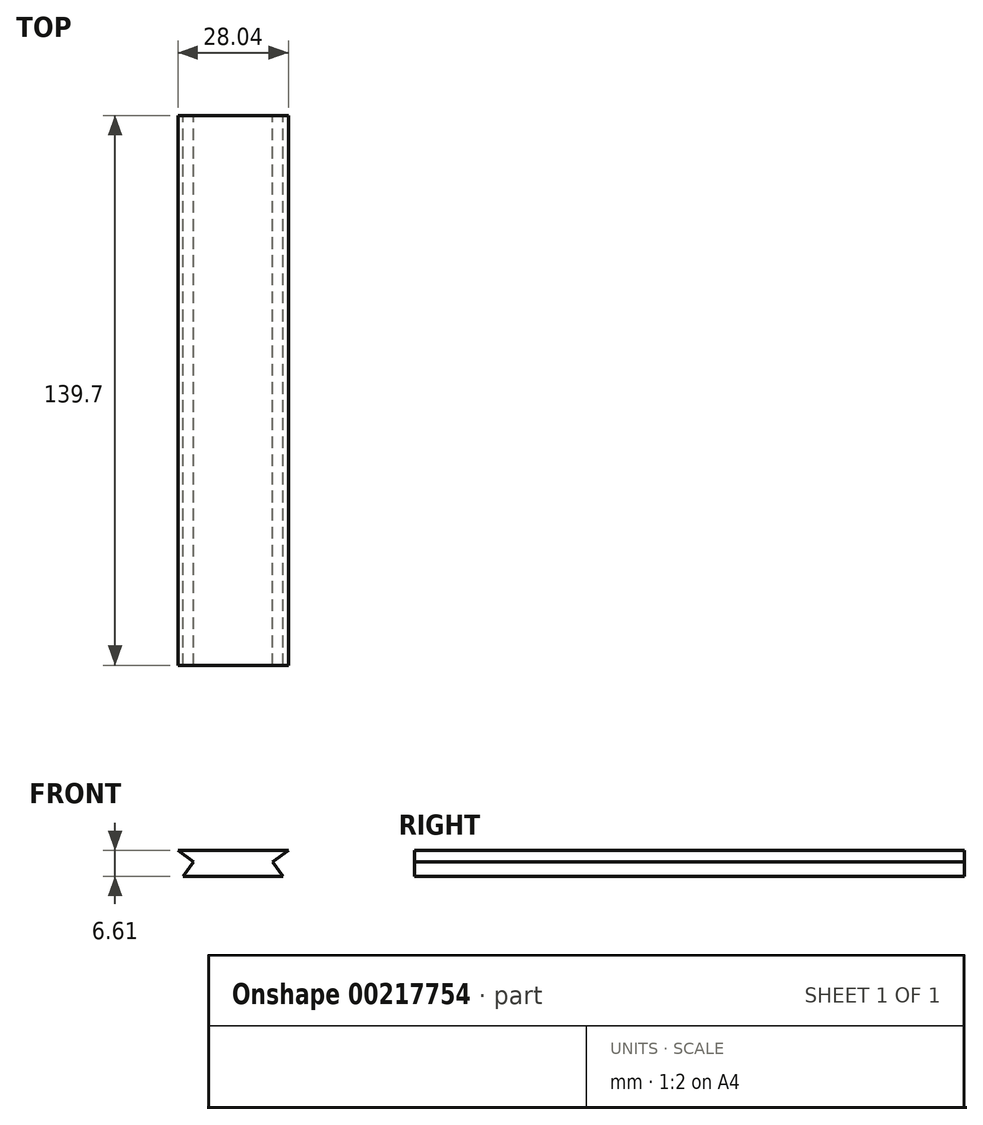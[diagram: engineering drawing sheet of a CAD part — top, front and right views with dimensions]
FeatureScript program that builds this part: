
annotation { "Feature Type Name" : "Feature", "Feature Type Description" : "" }
export const myFeature = defineFeature(function(context is Context, id is Id, definition is map)
    precondition{}
    {
        {
            var Q0;
            Q0=qCreatedBy(makeId("Front.planeOp"),FACE);
            var sketch = newSketch(context, id + "F0", { "sketchPlane" : qUnion([Q0])});
            skLineSegment(sketch, "E0", {"start": v(0, 0) * mm, "end": v(-12.7, 0) * mm});
            skLineSegment(sketch, "E1", {"start": v(-12.7, 0) * mm, "end": v(-10, 3.63) * mm});
            skLineSegment(sketch, "E2", {"start": v(-10, 3.63) * mm, "end": v(-14.02, 6.61) * mm});
            skLineSegment(sketch, "E3", {"start": v(-14.02, 6.61) * mm, "end": v(0, 6.61) * mm});
            skLineSegment(sketch, "E4.MirrorCS", {"start": v(12.7, 0) * mm, "end": v(10, 3.63) * mm});
            skLineSegment(sketch, "E5.MirrorCS", {"start": v(0, 0) * mm, "end": v(12.7, 0) * mm});
            skLineSegment(sketch, "E6.MirrorCS", {"start": v(10, 3.63) * mm, "end": v(14.02, 6.61) * mm});
            skLineSegment(sketch, "E7.MirrorCS", {"start": v(14.02, 6.61) * mm, "end": v(0, 6.61) * mm});
            skSolve(sketch);
        }
        {
            var Q0;
            Q0 = qSketchRegion(id + "F0", true);
            extrude(context, id + "F1", {"entities" : qUnion([Q0]), "depth" : 139.7 * mm});
        }
    });
